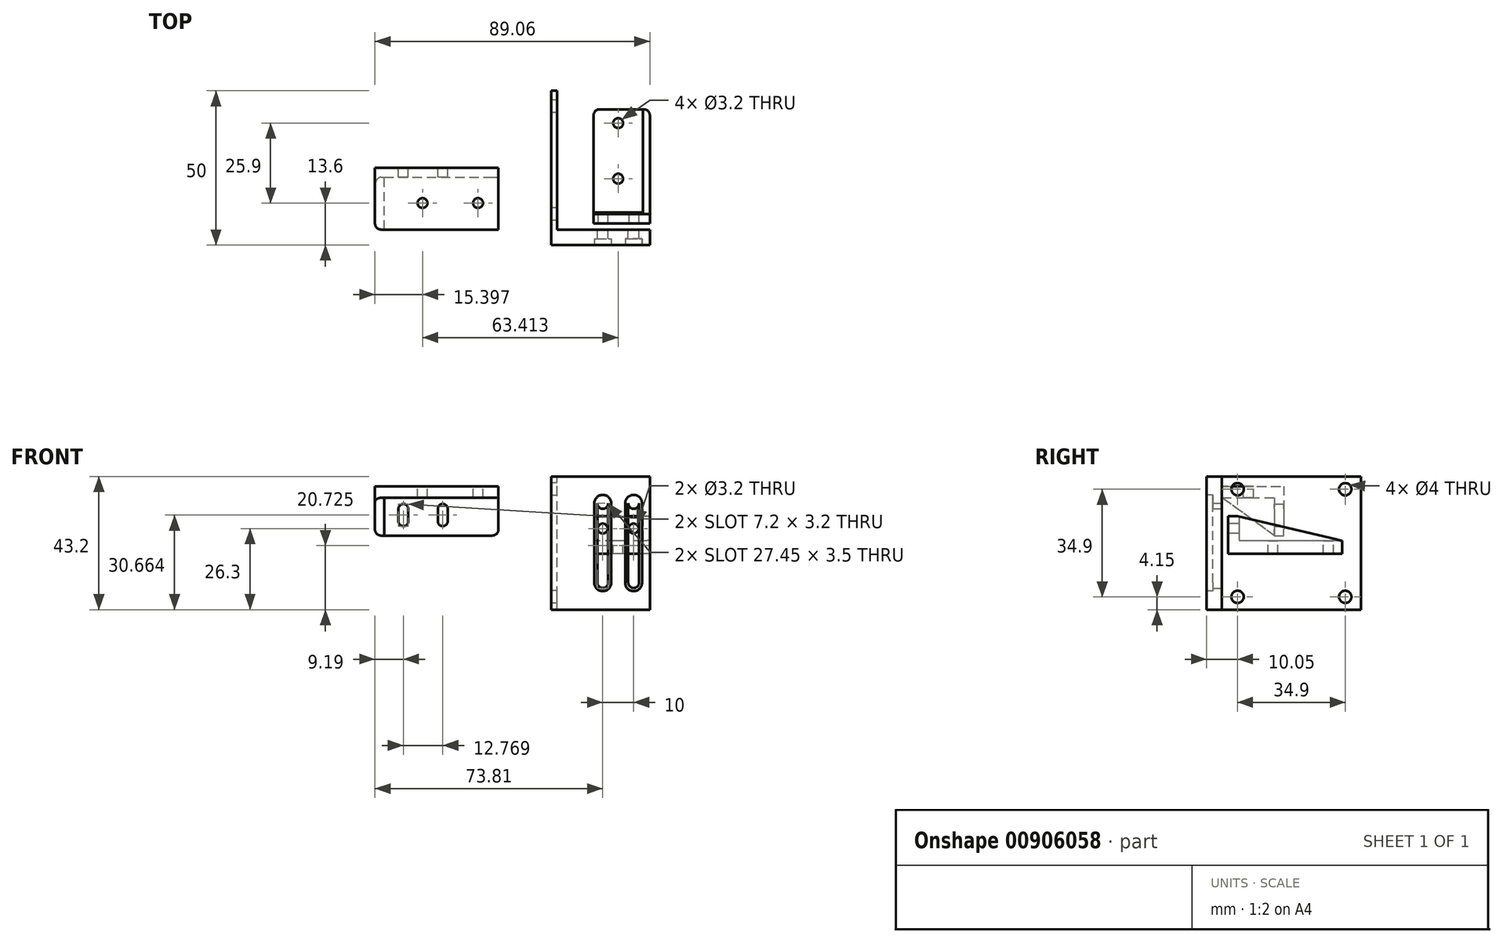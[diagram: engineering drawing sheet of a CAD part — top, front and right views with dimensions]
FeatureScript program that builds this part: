
annotation { "Feature Type Name" : "Feature", "Feature Type Description" : "" }
export const myFeature = defineFeature(function(context is Context, id is Id, definition is map)
    precondition{}
    {
        {
            var Q0;
            Q0=qCreatedBy(makeId("Right.planeOp"),FACE);
            var sketch = newSketch(context, id + "F0", { "sketchPlane" : qUnion([Q0])});
            skLineSegment(sketch, "E0.bottom", {"start": v(25, -21.6) * mm, "end": v(-25, -21.6) * mm});
            skLineSegment(sketch, "E0.top", {"start": v(25, 21.6) * mm, "end": v(-25, 21.6) * mm});
            skLineSegment(sketch, "E0.left", {"start": v(25, -21.6) * mm, "end": v(25, 21.6) * mm});
            skLineSegment(sketch, "E0.right", {"start": v(-25, -21.6) * mm, "end": v(-25, 21.6) * mm});
            skPoint(sketch, "E0.middle", {"position": v(0, 0) * mm});
            skLineSegment(sketch, "E1", {"start": v(-20, 0) * mm, "end": v(-20, -21.6) * mm});
            skLineSegment(sketch, "E2", {"start": v(-20, 0) * mm, "end": v(-20, 21.6) * mm});
            skCircle(sketch, "E3", {"center": v(-14.95, 17.45) * mm, "radius": 2 * mm});
            skCircle(sketch, "E4", {"center": v(19.95, 17.45) * mm, "radius": 2 * mm});
            skCircle(sketch, "E5", {"center": v(-14.95, -17.45) * mm, "radius": 2 * mm});
            skCircle(sketch, "E6", {"center": v(19.95, -17.45) * mm, "radius": 2 * mm});
            skPoint(sketch, "E7.endSnap0", {"position": v(-20, -10.8) * mm});
            skSolve(sketch);
        }
        {
            var Q0;
            {var subQ0=sQuery(id+"F0.wireOp",EDGE,"E0.left");Q0=makeQuery(id+"F0.imprint","IMPRINT",FACE,{"disambiguationData":[TD([[makeQuery(id+"F0.imprint","IMPRINT",EDGE,{"derivedFrom":subQ0}),1.0]])]});}
            extrude(context, id + "F1", {"entities" : qUnion([Q0]), "depth" : 2 * mm, "offsetDistance" : 25 * mm});
        }
        {
            var Q0;
            {var subQ0=sQuery(id+"F0.wireOp",EDGE,"E0.right");Q0=makeQuery(id+"F0.imprint","IMPRINT",FACE,{"disambiguationData":[TD([[makeQuery(id+"F0.imprint","IMPRINT",EDGE,{"derivedFrom":subQ0}),-1.0]])]});}
            extrude(context, id + "F2", {"entities" : qUnion([Q0]), "operationType" : NewBodyOperationType.ADD, "depth" : 32 * mm, "offsetDistance" : 25 * mm});
        }
        {
            var Q0;
            Q0=makeQuery(id+"F2.opExtrude","SWEPT_FACE",FACE,{"disambiguationData":[OSD([sQuery(id+"F0.wireOp",EDGE,"E1"),sQuery(id+"F0.wireOp",EDGE,"E2")])]});
            var sketch = newSketch(context, id + "F3", { "sketchPlane" : qUnion([Q0])});
            skCircle(sketch, "E8", {"center": v(-26.75, 12.85) * mm, "radius": 1.75 * mm});
            skCircle(sketch, "E9", {"center": v(-26.75, -12.85) * mm, "radius": 1.75 * mm});
            skCircle(sketch, "E10", {"center": v(-16.75, 12.85) * mm, "radius": 1.75 * mm});
            skCircle(sketch, "E11", {"center": v(-16.75, -12.85) * mm, "radius": 1.75 * mm});
            skLineSegment(sketch, "E12", {"start": v(-28.5, 12.85) * mm, "end": v(-28.5, -12.85) * mm});
            skLineSegment(sketch, "E13", {"start": v(-25, 12.85) * mm, "end": v(-25, -12.85) * mm});
            skLineSegment(sketch, "E14", {"start": v(-18.5, 12.85) * mm, "end": v(-18.5, -12.85) * mm});
            skLineSegment(sketch, "E15", {"start": v(-15, 12.85) * mm, "end": v(-15, -12.85) * mm});
            skSolve(sketch);
        }
        {
            var Q0;
            {var subQ0=sQuery(id+"F3.wireOp",EDGE,"E12");Q0=makeQuery(id+"F3.imprint","IMPRINT",FACE,{"disambiguationData":[TD([[makeQuery(id+"F3.imprint","IMPRINT",EDGE,{"derivedFrom":subQ0}),1.0]])]});}
            var Q1;
            {var subQ0=sQuery(id+"F3.wireOp",EDGE,"E8");var subQ2=makeQuery(id+"F3.imprint","IMPRINT",VERTEX,{"derivedFrom":subQ0});Q1=makeQuery(id+"F3.imprint","IMPRINT",FACE,{"disambiguationData":[TD([[makeQuery(id+"F3.imprint","IMPRINT",EDGE,{"disambiguationData":[TD([[subQ2,1.0]])],"derivedFrom":subQ0}),1.0]])]});}
            var Q2;
            {var subQ0=sQuery(id+"F3.wireOp",EDGE,"E9");var subQ1=makeQuery(id+"F3.imprint","INTERSECT",VERTEX,{"derivedFrom":[subQ0,sQuery(id+"F3.wireOp",EDGE,"E12")]});Q2=makeQuery(id+"F3.imprint","IMPRINT",FACE,{"disambiguationData":[TD([[makeQuery(id+"F3.imprint","IMPRINT",EDGE,{"disambiguationData":[TD([[subQ1,1.0]])],"derivedFrom":subQ0}),1.0]])]});}
            var Q3;
            {var subQ0=sQuery(id+"F3.wireOp",EDGE,"E14");Q3=makeQuery(id+"F3.imprint","IMPRINT",FACE,{"disambiguationData":[TD([[makeQuery(id+"F3.imprint","IMPRINT",EDGE,{"derivedFrom":subQ0}),1.0]])]});}
            var Q4;
            {var subQ0=sQuery(id+"F3.wireOp",EDGE,"E11");var subQ1=makeQuery(id+"F3.imprint","INTERSECT",VERTEX,{"derivedFrom":[subQ0,sQuery(id+"F3.wireOp",EDGE,"E14")]});Q4=makeQuery(id+"F3.imprint","IMPRINT",FACE,{"disambiguationData":[TD([[makeQuery(id+"F3.imprint","IMPRINT",EDGE,{"disambiguationData":[TD([[subQ1,1.0]])],"derivedFrom":subQ0}),1.0]])]});}
            var Q5;
            {var subQ0=sQuery(id+"F3.wireOp",EDGE,"E10");var subQ2=makeQuery(id+"F3.imprint","IMPRINT",VERTEX,{"derivedFrom":subQ0});Q5=makeQuery(id+"F3.imprint","IMPRINT",FACE,{"disambiguationData":[TD([[makeQuery(id+"F3.imprint","IMPRINT",EDGE,{"disambiguationData":[TD([[subQ2,1.0]])],"derivedFrom":subQ0}),1.0]])]});}
            extrude(context, id + "F4", {"entities" : qUnion([Q0, Q1, Q2, Q3, Q4, Q5]), "operationType" : NewBodyOperationType.REMOVE, "oppositeDirection" : true, "depth" : 25 * mm, "offsetDistance" : 25 * mm});
        }
        {
            var Q0;
            Q0=makeQuery(id+"F2.opExtrude","SWEPT_FACE",FACE,{"disambiguationData":[OSD([sQuery(id+"F0.wireOp",EDGE,"E0.right")])]});
            var sketch = newSketch(context, id + "F5", { "sketchPlane" : qUnion([Q0])});
            skArc(sketch, "E16.0", {"start": v(14, -12.85) * mm, "mid": v(16.75, -15.6) * mm, "end": v(19.5, -12.85) * mm});
            skLineSegment(sketch, "E16.1", {"start": v(14, -12.85) * mm, "end": v(14, 12.85) * mm});
            skArc(sketch, "E16.2", {"start": v(19.5, 12.85) * mm, "mid": v(16.75, 15.6) * mm, "end": v(14, 12.85) * mm});
            skLineSegment(sketch, "E16.3", {"start": v(19.5, -12.85) * mm, "end": v(19.5, 12.85) * mm});
            skLineSegment(sketch, "E17.0", {"start": v(29.5, -12.85) * mm, "end": v(29.5, 12.85) * mm});
            skArc(sketch, "E17.1", {"start": v(24, -12.85) * mm, "mid": v(26.75, -15.6) * mm, "end": v(29.5, -12.85) * mm});
            skLineSegment(sketch, "E17.2", {"start": v(24, -12.85) * mm, "end": v(24, 12.82) * mm});
            skArc(sketch, "E18.2", {"start": v(29.5, 12.85) * mm, "mid": v(26.74, 15.6) * mm, "end": v(24, 12.82) * mm});
            skSolve(sketch);
        }
        {
            var Q0;
            Q0=makeQuery(id+"F5.imprint","IMPRINT",FACE,{"disambiguationData":[TD([[makeQuery(id+"F5.imprint","IMPRINT",EDGE,{"derivedFrom":sQuery(id+"F5.wireOp",EDGE,"E16.0")}),1.0]])]});
            var Q1;
            Q1=makeQuery(id+"F5.imprint","IMPRINT",FACE,{"disambiguationData":[TD([[makeQuery(id+"F5.imprint","IMPRINT",EDGE,{"derivedFrom":sQuery(id+"F5.wireOp",EDGE,"E17.0")}),1.0]])]});
            extrude(context, id + "F6", {"entities" : qUnion([Q0, Q1]), "operationType" : NewBodyOperationType.REMOVE, "oppositeDirection" : true, "depth" : 2 * mm, "offsetDistance" : 25 * mm});
        }
        {
            var Q0;
            Q0=makeQuery(id+"F2.opExtrude","SWEPT_FACE",FACE,{"disambiguationData":[OSD([sQuery(id+"F0.wireOp",EDGE,"E1"),sQuery(id+"F0.wireOp",EDGE,"E2")])]});
            cPlane(context, id + "F7", {"entities" : qUnion([Q0]), "cplaneType" : CPlaneType.OFFSET, "offset" : 2 * mm, "width" : 150 * mm, "height" : 150 * mm});
        }
        {
            var Q0;
            Q0=qCreatedBy(id+"F7.planeOp",FACE);
            var sketch = newSketch(context, id + "F8", { "sketchPlane" : qUnion([Q0])});
            skLineSegment(sketch, "E19.bottom", {"start": v(-29.75, 8.7) * mm, "end": v(-13.75, 8.7) * mm});
            skLineSegment(sketch, "E19.top", {"start": v(-29.75, 0.7) * mm, "end": v(-13.75, 0.7) * mm});
            skLineSegment(sketch, "E19.left", {"start": v(-29.75, 8.7) * mm, "end": v(-29.75, 0.7) * mm});
            skLineSegment(sketch, "E19.right", {"start": v(-13.75, 8.7) * mm, "end": v(-13.75, 0.7) * mm});
            skLineSegment(sketch, "E20.top", {"start": v(-29.75, -3.5) * mm, "end": v(-13.75, -3.5) * mm});
            skLineSegment(sketch, "E20.left", {"start": v(-29.75, 0.7) * mm, "end": v(-29.75, -3.5) * mm});
            skLineSegment(sketch, "E20.right", {"start": v(-13.75, 0.7) * mm, "end": v(-13.75, -3.5) * mm});
            skCircle(sketch, "E21", {"center": v(-26.75, 4.7) * mm, "radius": 1.6 * mm});
            skCircle(sketch, "E22", {"center": v(-16.75, 4.7) * mm, "radius": 1.6 * mm});
            skLineSegment(sketch, "E23.bottom", {"start": v(-29.75, -3.5) * mm, "end": v(-32, -3.5) * mm});
            skLineSegment(sketch, "E23.top", {"start": v(-29.75, 8.7) * mm, "end": v(-32, 8.7) * mm});
            skLineSegment(sketch, "E23.left", {"start": v(-29.75, -3.5) * mm, "end": v(-29.75, 8.7) * mm});
            skLineSegment(sketch, "E23.right", {"start": v(-32, -3.5) * mm, "end": v(-32, 8.7) * mm});
            skSolve(sketch);
        }
        {
            var Q0;
            Q0=makeQuery(id+"F8.imprint","IMPRINT",FACE,{"disambiguationData":[TD([[makeQuery(id+"F8.imprint","IMPRINT",EDGE,{"derivedFrom":sQuery(id+"F8.wireOp",EDGE,"E20.top")}),1.0]])]});
            var Q1;
            {var subQ3=sQuery(id+"F8.wireOp",EDGE,"E23.bottom");Q1=makeQuery(id+"F8.imprint","IMPRINT",FACE,{"disambiguationData":[TD([[makeQuery(id+"F8.imprint","IMPRINT",EDGE,{"derivedFrom":subQ3}),-1.0]])]});}
            extrude(context, id + "F9", {"entities" : qUnion([Q0, Q1]), "depth" : 37 * mm, "offsetDistance" : 25 * mm});
        }
        {
            var Q0;
            {var subQ1=sQuery(id+"F8.wireOp",EDGE,"E19.left");Q0=makeQuery(id+"F8.imprint","IMPRINT",FACE,{"disambiguationData":[TD([[makeQuery(id+"F8.imprint","IMPRINT",EDGE,{"derivedFrom":subQ1}),1.0]])]});}
            var Q1;
            {var subQ1=sQuery(id+"F8.wireOp",EDGE,"E19.right");Q1=makeQuery(id+"F8.imprint","IMPRINT",FACE,{"disambiguationData":[TD([[makeQuery(id+"F8.imprint","IMPRINT",EDGE,{"derivedFrom":subQ1}),-1.0]])]});}
            extrude(context, id + "F10", {"entities" : qUnion([Q0, Q1]), "operationType" : NewBodyOperationType.ADD, "depth" : 3.5 * mm, "offsetDistance" : 25 * mm});
        }
        {
            var Q0;
            Q0=makeQuery(id+"F9.opExtrude","CAP_EDGE",EDGE,{"disambiguationData":[OSD([sQuery(id+"F8.wireOp",EDGE,"E23.top")])],"isStart":false});
            chamfer(context, id + "F11", {"entities" : qUnion([Q0]), "chamferType" : ChamferType.TWO_OFFSETS, "width1" : 8 * mm, "oppositeDirection" : false, "width2" : 34 * mm, "tangentPropagation" : true});
        }
        {
            var Q0;
            Q0=makeQuery(id+"F9.opExtrude","SWEPT_FACE",FACE,{"disambiguationData":[OSD([sQuery(id+"F8.wireOp",EDGE,"E19.top")])]});
            var sketch = newSketch(context, id + "F12", { "sketchPlane" : qUnion([Q0])});
            skCircle(sketch, "E24", {"center": v(21.75, -3.5) * mm, "radius": 1.6 * mm});
            skCircle(sketch, "E25", {"center": v(21.75, 14.5) * mm, "radius": 1.6 * mm});
            skSolve(sketch);
        }
        {
            var Q0;
            Q0=makeQuery(id+"F12.imprint","IMPRINT",FACE,{"disambiguationData":[TD([[makeQuery(id+"F12.imprint","IMPRINT",EDGE,{"derivedFrom":sQuery(id+"F12.wireOp",EDGE,"E24")}),1.0]])]});
            var Q1;
            Q1=makeQuery(id+"F12.imprint","IMPRINT",FACE,{"disambiguationData":[TD([[makeQuery(id+"F12.imprint","IMPRINT",EDGE,{"derivedFrom":sQuery(id+"F12.wireOp",EDGE,"E25")}),1.0]])]});
            extrude(context, id + "F13", {"entities" : qUnion([Q0, Q1]), "operationType" : NewBodyOperationType.REMOVE, "oppositeDirection" : true, "depth" : 5 * mm, "offsetDistance" : 25 * mm});
        }
        {
            var Q0;
            Q0=makeQuery(id+"F9.opExtrude","CAP_EDGE",EDGE,{"disambiguationData":[OSD([sQuery(id+"F8.wireOp",EDGE,"E20.right")])],"isStart":false});
            var Q1;
            Q1=makeQuery(id+"F9.opExtrude","CAP_EDGE",EDGE,{"disambiguationData":[OSD([sQuery(id+"F8.wireOp",EDGE,"E23.right")])],"isStart":false});
            fillet(context, id + "F14", {"entities" : qUnion([Q0, Q1]), "radius" : 2 * mm, "tangentPropagation" : true, "allowEdgeOverflow" : false});
        }
        {
            var Q0;
            Q0=qCreatedBy(makeId("Front.planeOp"),FACE);
            var sketch = newSketch(context, id + "F15", { "sketchPlane" : qUnion([Q0])});
            skLineSegment(sketch, "E26.bottom", {"start": v(-54.06, 18.41) * mm, "end": v(-17.06, 18.41) * mm});
            skLineSegment(sketch, "E26.top", {"start": v(-54.06, 2.41) * mm, "end": v(-17.06, 2.41) * mm});
            skLineSegment(sketch, "E26.left", {"start": v(-54.06, 18.41) * mm, "end": v(-54.06, 2.41) * mm});
            skLineSegment(sketch, "E26.right", {"start": v(-17.06, 18.41) * mm, "end": v(-17.06, 2.41) * mm});
            skLineSegment(sketch, "E27.top", {"start": v(-54.06, 14.66) * mm, "end": v(-17.06, 14.66) * mm});
            skLineSegment(sketch, "E27.left", {"start": v(-54.06, 18.41) * mm, "end": v(-54.06, 14.66) * mm});
            skLineSegment(sketch, "E27.right", {"start": v(-17.06, 18.41) * mm, "end": v(-17.06, 14.66) * mm});
            skCircle(sketch, "E28", {"center": v(-47.87, 11.06) * mm, "radius": 1.6 * mm});
            skCircle(sketch, "E29", {"center": v(-47.87, 7.06) * mm, "radius": 1.6 * mm});
            skLineSegment(sketch, "E30.bottom", {"start": v(-49.47, 11.06) * mm, "end": v(-46.27, 11.06) * mm});
            skLineSegment(sketch, "E30.top", {"start": v(-49.47, 7.06) * mm, "end": v(-46.27, 7.06) * mm});
            skLineSegment(sketch, "E30.left", {"start": v(-49.47, 11.06) * mm, "end": v(-49.47, 7.06) * mm});
            skLineSegment(sketch, "E30.right", {"start": v(-46.27, 11.06) * mm, "end": v(-46.27, 7.06) * mm});
            skCircle(sketch, "E31", {"center": v(-35.1, 11.06) * mm, "radius": 1.6 * mm});
            skCircle(sketch, "E32", {"center": v(-35.1, 7.06) * mm, "radius": 1.6 * mm});
            skLineSegment(sketch, "E33.bottom", {"start": v(-36.7, 11.06) * mm, "end": v(-33.5, 11.06) * mm});
            skLineSegment(sketch, "E33.top", {"start": v(-36.7, 7.06) * mm, "end": v(-33.5, 7.06) * mm});
            skLineSegment(sketch, "E33.left", {"start": v(-36.7, 11.06) * mm, "end": v(-36.7, 7.06) * mm});
            skLineSegment(sketch, "E33.right", {"start": v(-33.5, 11.06) * mm, "end": v(-33.5, 7.06) * mm});
            skSolve(sketch);
        }
        {
            var Q0;
            Q0=makeQuery(id+"F15.imprint","IMPRINT",FACE,{"disambiguationData":[TD([[makeQuery(id+"F15.imprint","IMPRINT",EDGE,{"derivedFrom":sQuery(id+"F15.wireOp",EDGE,"E26.top")}),1.0]])]});
            extrude(context, id + "F16", {"entities" : qUnion([Q0]), "depth" : 3 * mm, "offsetDistance" : 25 * mm});
        }
        {
            var Q0;
            Q0=makeQuery(id+"F15.imprint","IMPRINT",FACE,{"disambiguationData":[TD([[makeQuery(id+"F15.imprint","IMPRINT",EDGE,{"derivedFrom":sQuery(id+"F15.wireOp",EDGE,"E26.bottom")}),-1.0]])]});
            extrude(context, id + "F17", {"entities" : qUnion([Q0]), "operationType" : NewBodyOperationType.ADD, "depth" : 20 * mm, "offsetDistance" : 25 * mm});
        }
        {
            var Q0;
            Q0=makeQuery(id+"F17.opExtrude","SWEPT_FACE",FACE,{"disambiguationData":[OSD([sQuery(id+"F15.wireOp",EDGE,"E26.bottom")])]});
            var sketch = newSketch(context, id + "F18", { "sketchPlane" : qUnion([Q0])});
            skCircle(sketch, "E34", {"center": v(-41.66, -11.4) * mm, "radius": 1.6 * mm});
            skCircle(sketch, "E35", {"center": v(-23.66, -11.4) * mm, "radius": 1.6 * mm});
            skSolve(sketch);
        }
        {
            var Q0;
            Q0=makeQuery(id+"F18.imprint","IMPRINT",FACE,{"disambiguationData":[TD([[makeQuery(id+"F18.imprint","IMPRINT",EDGE,{"derivedFrom":sQuery(id+"F18.wireOp",EDGE,"E34")}),1.0]])]});
            var Q1;
            Q1=makeQuery(id+"F18.imprint","IMPRINT",FACE,{"disambiguationData":[TD([[makeQuery(id+"F18.imprint","IMPRINT",EDGE,{"derivedFrom":sQuery(id+"F18.wireOp",EDGE,"E35")}),1.0]])]});
            extrude(context, id + "F19", {"entities" : qUnion([Q0, Q1]), "operationType" : NewBodyOperationType.REMOVE, "oppositeDirection" : true, "depth" : 25 * mm, "offsetDistance" : 25 * mm});
        }
        {
            var Q0;
            Q0=makeQuery(id+"F17.boolean.opBoolean","MERGE",FACE,{"derivedFrom":[makeQuery(id+"F16.opExtrude","SWEPT_FACE",FACE,{"disambiguationData":[OSD([sQuery(id+"F15.wireOp",EDGE,"E26.left")])]}),makeQuery(id+"F17.opExtrude","SWEPT_FACE",FACE,{"disambiguationData":[OSD([sQuery(id+"F15.wireOp",EDGE,"E27.left")])]})]});
            var sketch = newSketch(context, id + "F20", { "sketchPlane" : qUnion([Q0])});
            skLineSegment(sketch, "E36", {"start": v(0, 18.41) * mm, "end": v(0, 2.41) * mm});
            skLineSegment(sketch, "E37", {"start": v(0, 2.41) * mm, "end": v(3, 2.41) * mm});
            skLineSegment(sketch, "E38", {"start": v(3, 2.41) * mm, "end": v(20, 14.66) * mm});
            skLineSegment(sketch, "E39", {"start": v(20, 14.66) * mm, "end": v(20, 18.41) * mm});
            skLineSegment(sketch, "E40", {"start": v(20, 18.41) * mm, "end": v(0, 18.41) * mm});
            skSolve(sketch);
        }
        {
            var Q0;
            Q0=makeQuery(id+"F20.imprint","IMPRINT",FACE,{"disambiguationData":[TD([[makeQuery(id+"F20.imprint","IMPRINT",EDGE,{"derivedFrom":sQuery(id+"F20.wireOp",EDGE,"E38")}),1.0]])]});
            var Q1;
            Q1=makeQuery(id+"F20.imprint","IMPRINT",FACE,{"disambiguationData":[TD([[makeQuery(id+"F20.imprint","IMPRINT",EDGE,{"derivedFrom":sQuery(id+"F20.wireOp",EDGE,"E36")}),1.0]])]});
            extrude(context, id + "F21", {"entities" : qUnion([Q0, Q1]), "operationType" : NewBodyOperationType.ADD, "depth" : 3 * mm, "offsetDistance" : 25 * mm});
        }
        {
            var Q0;
            Q0=makeQuery(id+"F21.opExtrude","CAP_EDGE",EDGE,{"disambiguationData":[OSD([sQuery(id+"F20.wireOp",EDGE,"E37")])],"isStart":false});
            var Q1;
            Q1=makeQuery(id+"F21.opExtrude","CAP_EDGE",EDGE,{"disambiguationData":[OSD([sQuery(id+"F20.wireOp",EDGE,"E39")])],"isStart":false});
            var Q2;
            Q2=makeQuery(id+"F17.opExtrude","CAP_EDGE",EDGE,{"disambiguationData":[OSD([sQuery(id+"F15.wireOp",EDGE,"E27.right")])],"isStart":false});
            var Q3;
            Q3=makeQuery(id+"F16.opExtrude","SWEPT_EDGE",EDGE,{"disambiguationData":[OSD([sQuery(id+"F15.wireOp",EDGE,"E26.top"),sQuery(id+"F15.wireOp",EDGE,"E26.right")])]});
            fillet(context, id + "F22", {"entities" : qUnion([Q0, Q1, Q2, Q3]), "radius" : 2 * mm, "tangentPropagation" : true, "allowEdgeOverflow" : false});
        }
    });
